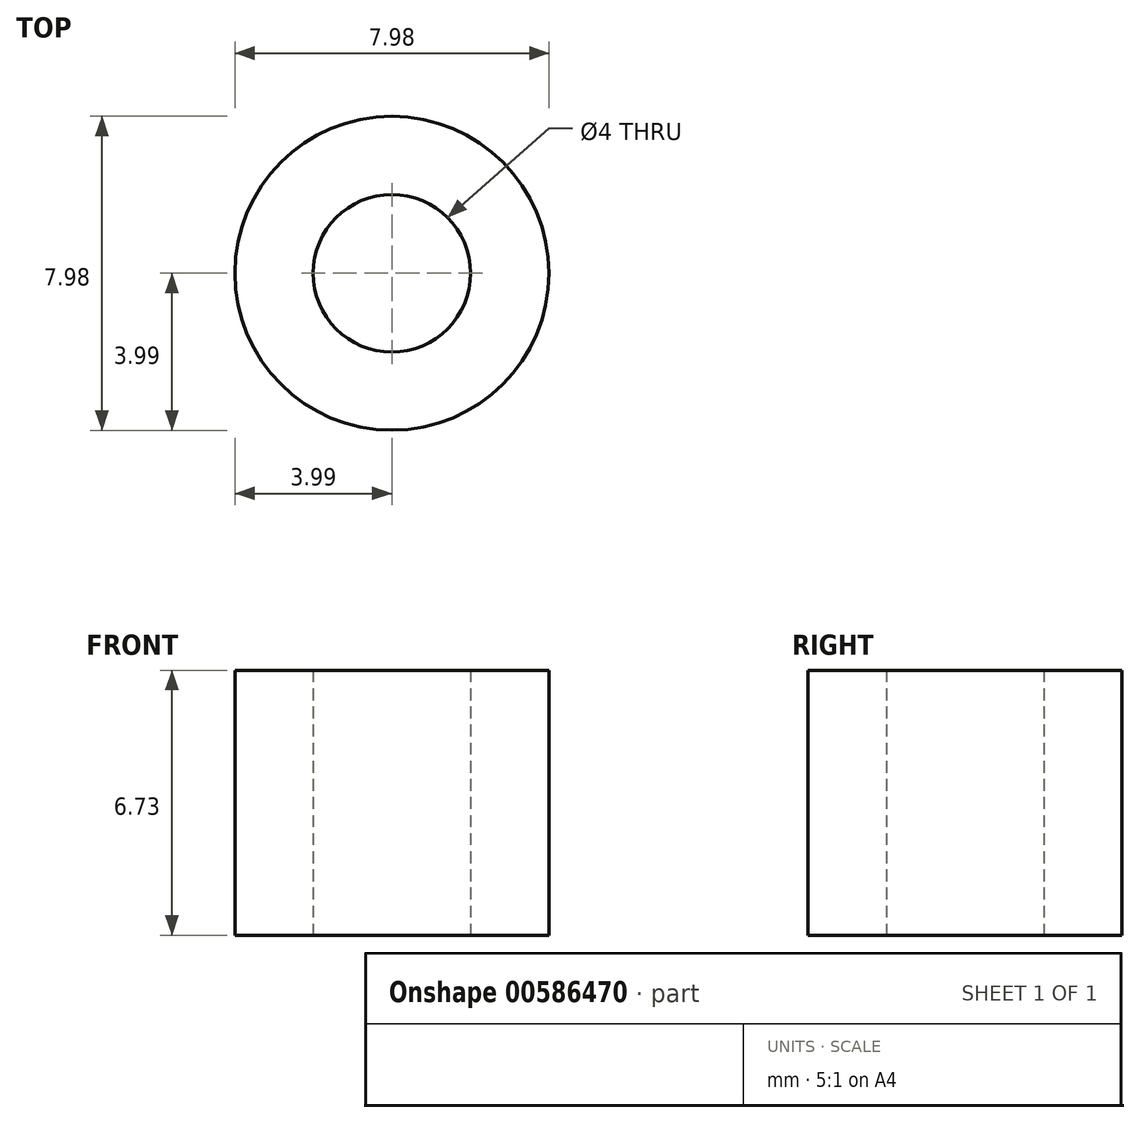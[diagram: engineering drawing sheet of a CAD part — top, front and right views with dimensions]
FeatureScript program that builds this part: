
annotation { "Feature Type Name" : "Feature", "Feature Type Description" : "" }
export const myFeature = defineFeature(function(context is Context, id is Id, definition is map)
    precondition{}
    {
        {
            var Q0;
            Q0=qCreatedBy(makeId("Top.planeOp"),FACE);
            var sketch = newSketch(context, id + "F0", { "sketchPlane" : qUnion([Q0])});
            skCircle(sketch, "E0", {"center": v(0, 0) * mm, "radius": 3.99 * mm});
            skCircle(sketch, "E1", {"center": v(0, 0) * mm, "radius": 2 * mm});
            skSolve(sketch);
        }
        {
            var Q0;
            Q0=makeQuery(id+"F0.imprint","IMPRINT",FACE,{"disambiguationData":[TD([[makeQuery(id+"F0.imprint","IMPRINT",EDGE,{"derivedFrom":sQuery(id+"F0.wireOp",EDGE,"E0")}),1.0]])]});
            extrude(context, id + "F1", {"entities" : qUnion([Q0]), "depth" : 6.73 * mm, "offsetDistance" : 25.4 * mm});
        }
    });
